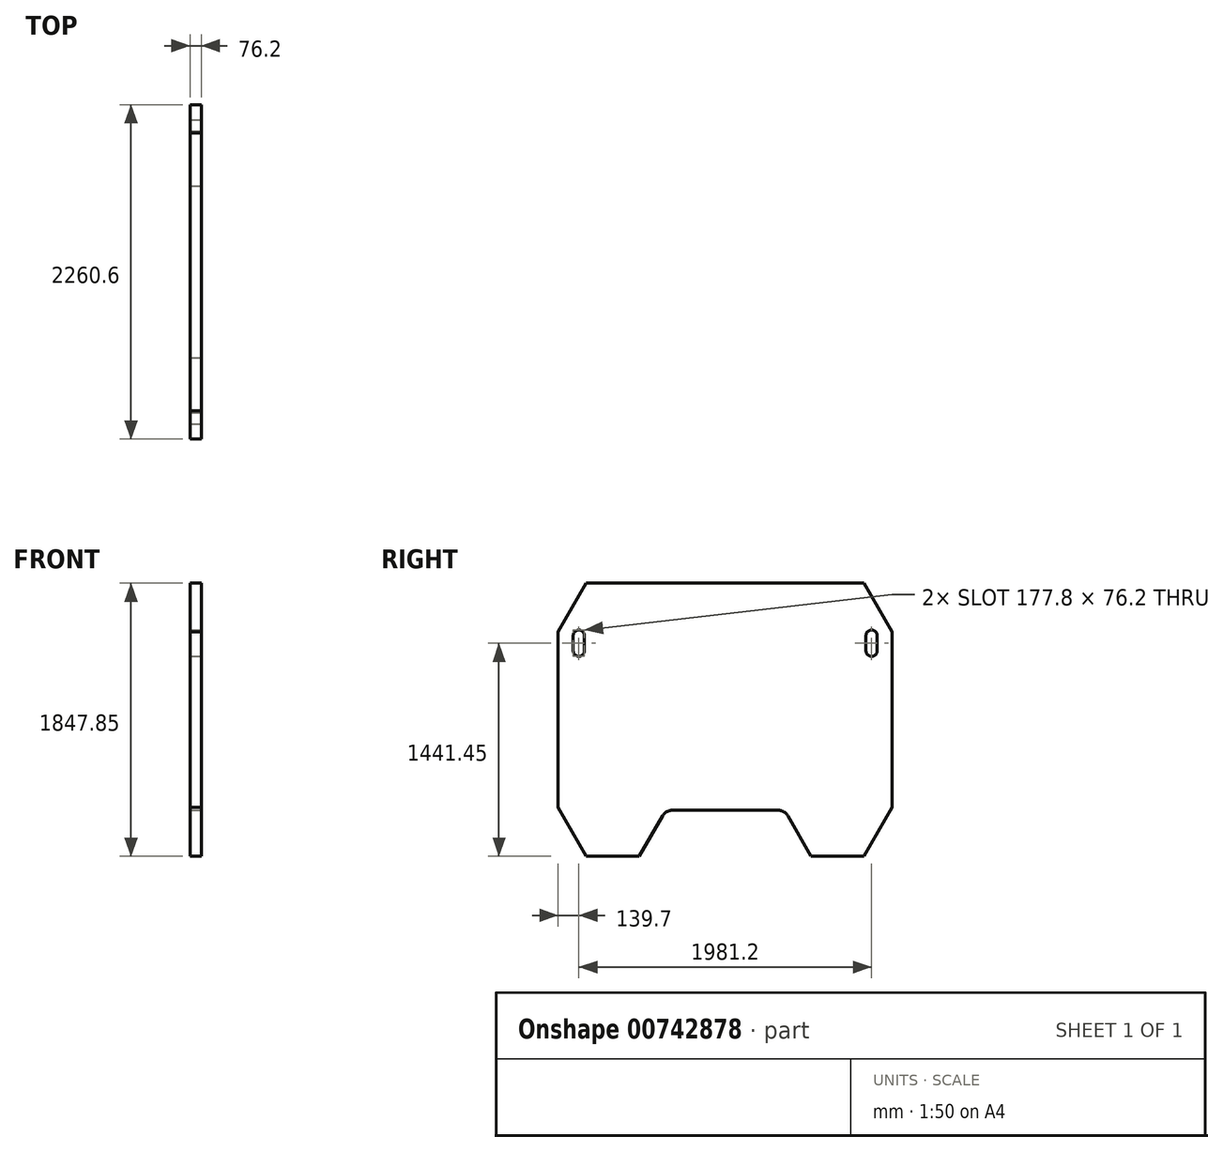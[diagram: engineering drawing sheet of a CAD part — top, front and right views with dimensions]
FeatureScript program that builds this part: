
annotation { "Feature Type Name" : "Feature", "Feature Type Description" : "" }
export const myFeature = defineFeature(function(context is Context, id is Id, definition is map)
    precondition{}
    {
        {
            var Q0;
            Q0=qCreatedBy(makeId("Right.planeOp"),FACE);
            var sketch = newSketch(context, id + "F0", { "sketchPlane" : qUnion([Q0])});
            skLineSegment(sketch, "E0.bottom", {"start": v(-939.8, 923.92) * mm, "end": v(939.8, 923.92) * mm});
            skLineSegment(sketch, "E0.top", {"start": v(-939.8, -923.93) * mm, "end": v(939.8, -923.93) * mm});
            skLineSegment(sketch, "E0.left", {"start": v(-1130.3, 593.97) * mm, "end": v(-1130.3, -593.97) * mm});
            skLineSegment(sketch, "E0.right", {"start": v(1130.3, 593.97) * mm, "end": v(1130.3, -593.97) * mm});
            skPoint(sketch, "E0.middle", {"position": v(0, 0) * mm});
            skLineSegment(sketch, "E1.0", {"start": v(939.8, 923.92) * mm, "end": v(939.8, -923.93) * mm, "construction": true});
            skLineSegment(sketch, "E2", {"start": v(0, 1115.42) * mm, "end": v(0, -1189.36) * mm, "construction": true});
            skPoint(sketch, "E2.endSnap0", {"position": v(0, -923.93) * mm});
            skLineSegment(sketch, "E3", {"start": v(939.8, -923.93) * mm, "end": v(1130.3, -593.97) * mm});
            skLineSegment(sketch, "E4", {"start": v(-1896.46, 0) * mm, "end": v(1811.22, 0) * mm, "construction": true});
            skLineSegment(sketch, "E5.MirrorCS", {"start": v(939.8, 923.93) * mm, "end": v(1130.3, 593.97) * mm});
            skLineSegment(sketch, "E6.MirrorCS", {"start": v(-939.8, 923.93) * mm, "end": v(-1130.3, 593.97) * mm});
            skLineSegment(sketch, "E7.MirrorCS", {"start": v(-939.8, -923.93) * mm, "end": v(-1130.3, -593.97) * mm});
            skPoint(sketch, "E8.orphan", {"position": v(-1269.93, 352.13) * mm});
            skPoint(sketch, "E9.orphan", {"position": v(-1130.3, 923.92) * mm});
            skPoint(sketch, "E10.orphan", {"position": v(1130.3, 923.92) * mm});
            skPoint(sketch, "E11.orphan", {"position": v(1269.93, 352.13) * mm});
            skPoint(sketch, "E12.orphan", {"position": v(1269.93, -352.13) * mm});
            skPoint(sketch, "E13.orphan", {"position": v(1130.3, -923.93) * mm});
            skPoint(sketch, "E14.orphan", {"position": v(-1130.3, -923.93) * mm});
            skPoint(sketch, "E15.orphan", {"position": v(-1269.93, -352.13) * mm});
            skLineSegment(sketch, "E16", {"start": v(939.8, 923.92) * mm, "end": v(1492.5, 923.92) * mm, "construction": true});
            skLineSegment(sketch, "E17.0", {"start": v(990.6, 593.97) * mm, "end": v(990.6, -593.97) * mm, "construction": true});
            skLineSegment(sketch, "E18.0", {"start": v(939.8, 568.32) * mm, "end": v(1492.5, 568.33) * mm, "construction": true});
            skLineSegment(sketch, "E19.0", {"start": v(939.8, 466.72) * mm, "end": v(1492.5, 466.73) * mm, "construction": true});
            skArc(sketch, "E20", {"start": v(1028.7, 568.32) * mm, "mid": v(990.6, 606.42) * mm, "end": v(952.5, 568.32) * mm});
            skArc(sketch, "E21", {"start": v(952.5, 466.72) * mm, "mid": v(990.6, 428.62) * mm, "end": v(1028.7, 466.72) * mm});
            skLineSegment(sketch, "E22", {"start": v(1028.7, 568.32) * mm, "end": v(1028.7, 466.72) * mm});
            skLineSegment(sketch, "E23", {"start": v(952.5, 466.72) * mm, "end": v(952.5, 568.32) * mm});
            skLineSegment(sketch, "E24.MirrorCS", {"start": v(939.8, 923.92) * mm, "end": v(-939.8, 923.93) * mm});
            skArc(sketch, "E25.MirrorCS", {"start": v(-1028.7, 568.33) * mm, "mid": v(-990.6, 606.43) * mm, "end": v(-952.5, 568.33) * mm});
            skArc(sketch, "E26.MirrorCS", {"start": v(-952.5, 466.73) * mm, "mid": v(-990.6, 428.63) * mm, "end": v(-1028.7, 466.73) * mm});
            skLineSegment(sketch, "E27.MirrorCS", {"start": v(-952.5, 466.73) * mm, "end": v(-952.5, 568.33) * mm});
            skLineSegment(sketch, "E28.MirrorCS", {"start": v(-1028.7, 568.33) * mm, "end": v(-1028.7, 466.73) * mm});
            skSolve(sketch);
        }
        {
            var Q0;
            Q0 = qSketchRegion(id + "F0", true);
            extrude(context, id + "F1", {"entities" : qUnion([Q0]), "endBound" : BoundingType.SYMMETRIC, "oppositeDirection" : true, "depth" : 76.2 * mm, "offsetDistance" : 25.4 * mm});
        }
        {
            var Q0;
            Q0=makeQuery(id+"F1.opExtrude","CAP_FACE",FACE,{"disambiguationData":[OSD([sQuery(id+"F0.wireOp",EDGE,"E0.top"),sQuery(id+"F0.wireOp",EDGE,"E0.left"),sQuery(id+"F0.wireOp",EDGE,"E0.right"),sQuery(id+"F0.wireOp",EDGE,"E3"),sQuery(id+"F0.wireOp",EDGE,"E5.MirrorCS"),sQuery(id+"F0.wireOp",EDGE,"E7.MirrorCS"),sQuery(id+"F0.wireOp",EDGE,"E20"),sQuery(id+"F0.wireOp",EDGE,"E21"),sQuery(id+"F0.wireOp",EDGE,"E22"),sQuery(id+"F0.wireOp",EDGE,"E23"),sQuery(id+"F0.wireOp",EDGE,"E24.MirrorCS"),sQuery(id+"F0.wireOp",EDGE,"E25.MirrorCS"),sQuery(id+"F0.wireOp",EDGE,"E26.MirrorCS"),sQuery(id+"F0.wireOp",EDGE,"E27.MirrorCS"),sQuery(id+"F0.wireOp",EDGE,"E6.MirrorCS"),sQuery(id+"F0.wireOp",EDGE,"E28.MirrorCS")])],"isStart":true});
            var sketch = newSketch(context, id + "F2", { "sketchPlane" : qUnion([Q0])});
            skLineSegment(sketch, "E29", {"start": v(0, 1175.36) * mm, "end": v(0, -1177.88) * mm, "construction": true});
            skLineSegment(sketch, "E30", {"start": v(939.8, -923.93) * mm, "end": v(939.8, -1305.98) * mm, "construction": true});
            skLineSegment(sketch, "E31.0", {"start": v(581.15, -923.93) * mm, "end": v(581.15, -1305.98) * mm, "construction": true});
            skLineSegment(sketch, "E32.0", {"start": v(-357.52, -612.78) * mm, "end": v(357.52, -612.78) * mm});
            skLineSegment(sketch, "E33.0", {"start": v(-939.8, -923.93) * mm, "end": v(939.8, -923.93) * mm});
            skLineSegment(sketch, "E34", {"start": v(581.15, -923.93) * mm, "end": v(423.5, -650.88) * mm});
            skLineSegment(sketch, "E35.MirrorCS", {"start": v(-581.15, -923.93) * mm, "end": v(-423.5, -650.87) * mm});
            skPoint(sketch, "E36.newPointA", {"position": v(-343.97, -513.12) * mm});
            skArc(sketch, "E36.filletArc", {"start": v(-357.52, -612.78) * mm, "mid": v(-395.62, -622.98) * mm, "end": v(-423.5, -650.88) * mm});
            skPoint(sketch, "E37.newPointB", {"position": v(343.97, -513.12) * mm});
            skArc(sketch, "E37.filletArc", {"start": v(423.5, -650.88) * mm, "mid": v(395.62, -622.98) * mm, "end": v(357.52, -612.78) * mm});
            skSolve(sketch);
        }
        {
            var Q0;
            Q0 = qSketchRegion(id + "F2", true);
            extrude(context, id + "F3", {"entities" : qUnion([Q0]), "operationType" : NewBodyOperationType.REMOVE, "endBound" : BoundingType.THROUGH_ALL, "oppositeDirection" : true, "depth" : 25.4 * mm, "offsetDistance" : 25.4 * mm});
        }
    });
